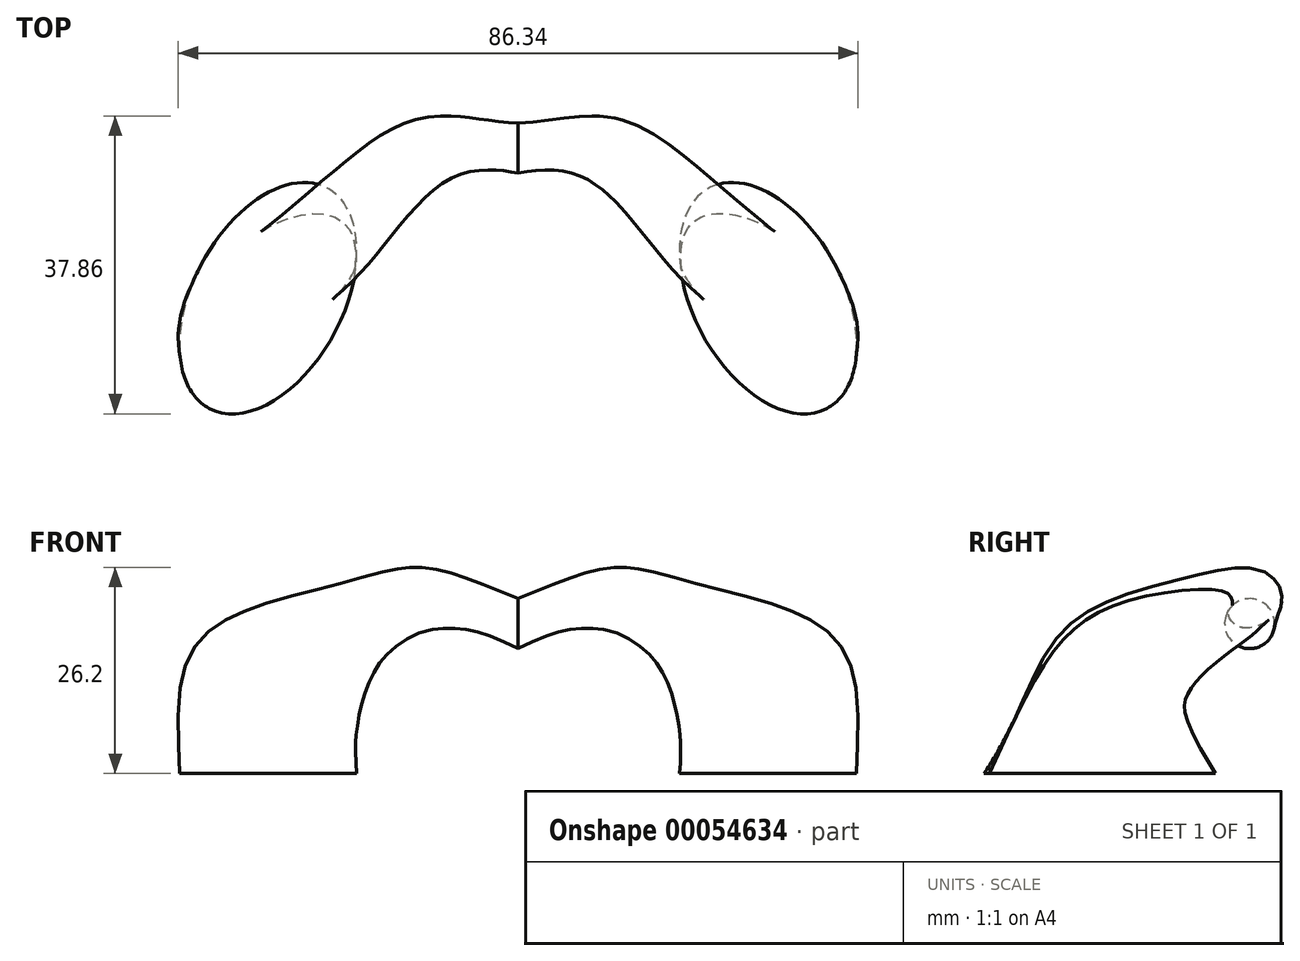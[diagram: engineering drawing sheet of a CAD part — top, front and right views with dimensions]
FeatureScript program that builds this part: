
annotation { "Feature Type Name" : "Feature", "Feature Type Description" : "" }
export const myFeature = defineFeature(function(context is Context, id is Id, definition is map)
    precondition{}
    {
        {
            var Q0;
            Q0=qCreatedBy(makeId("Top.planeOp"),FACE);
            var sketch = newSketch(context, id + "F0", { "sketchPlane" : qUnion([Q0])});
            skEllipse(sketch, "E0", {"center": v(31.75, -19.05) * mm, "majorRadius": 15.88 * mm, "minorRadius": 9.53 * mm, "majorAxis": v(0.47, -0.88)});
            skSolve(sketch);
        }
        {
            var Q0;
            Q0=qCreatedBy(makeId("Right.planeOp"),FACE);
            var sketch = newSketch(context, id + "F1", { "sketchPlane" : qUnion([Q0])});
            skCircle(sketch, "E1", {"center": v(0, 19.05) * mm, "radius": 3.18 * mm});
            skSolve(sketch);
        }
        {
            var Q0;
            Q0=qCreatedBy(makeId("Right.planeOp"),FACE);
            var Q1;
            Q1=qCreatedBy(makeId("Top.planeOp"),FACE);
            cPlane(context, id + "F2", {"entities" : qUnion([Q0, Q1]), "cplaneType" : CPlaneType.MID_PLANE, "offset" : 25.4 * mm, "width" : 152.4 * mm, "height" : 152.4 * mm});
        }
        {
            var Q0;
            Q0=qCreatedBy(id+"F2.planeOp",FACE);
            var sketch = newSketch(context, id + "F3", { "sketchPlane" : qUnion([Q0])});
            skEllipse(sketch, "E2", {"center": v(-7.75, 28.08) * mm, "majorRadius": 8.5 * mm, "minorRadius": 5.1 * mm, "majorAxis": v(-0.94, 0.35)});
            skSolve(sketch);
        }
        {
            var Q0;
            Q0=qCreatedBy(makeId("Right.planeOp"),FACE);
            var Q1;
            Q1=qCreatedBy(id+"F2.planeOp",FACE);
            cPlane(context, id + "F4", {"entities" : qUnion([Q0, Q1]), "cplaneType" : CPlaneType.MID_PLANE, "offset" : 152.4 * mm, "flipAlignment" : true, "width" : 152.4 * mm, "height" : 152.4 * mm});
        }
        {
            var Q0;
            Q0=qCreatedBy(id+"F4.planeOp",FACE);
            var sketch = newSketch(context, id + "F5", { "sketchPlane" : qUnion([Q0])});
            skCircle(sketch, "E3", {"center": v(0, 24.07) * mm, "radius": 4.1 * mm});
            skSolve(sketch);
        }
        {
            var Q0;
            Q0=qCreatedBy(id+"F2.planeOp",FACE);
            var Q1;
            Q1=qCreatedBy(makeId("Top.planeOp"),FACE);
            cPlane(context, id + "F6", {"entities" : qUnion([Q0, Q1]), "cplaneType" : CPlaneType.MID_PLANE, "offset" : 152.4 * mm, "width" : 152.4 * mm, "height" : 152.4 * mm});
        }
        {
            var Q0;
            Q0=qCreatedBy(id+"F6.planeOp",FACE);
            var sketch = newSketch(context, id + "F7", { "sketchPlane" : qUnion([Q0])});
            skEllipse(sketch, "E4", {"center": v(32.8, 16.93) * mm, "majorRadius": 12.65 * mm, "minorRadius": 6.7 * mm, "majorAxis": v(0.83, 0.56)});
            skSolve(sketch);
        }
        {
            var Q0;
            Q0=makeQuery(id+"F0.imprint","IMPRINT",FACE,{"disambiguationData":[TD([[makeQuery(id+"F0.imprint","IMPRINT",EDGE,{"derivedFrom":sQuery(id+"F0.wireOp",EDGE,"E0")}),1.0]])]});
            var Q1;
            Q1=makeQuery(id+"F7.imprint","IMPRINT",FACE,{"disambiguationData":[TD([[makeQuery(id+"F7.imprint","IMPRINT",EDGE,{"derivedFrom":sQuery(id+"F7.wireOp",EDGE,"E4")}),1.0]])]});
            var Q2;
            Q2=makeQuery(id+"F3.imprint","IMPRINT",FACE,{"disambiguationData":[TD([[makeQuery(id+"F3.imprint","IMPRINT",EDGE,{"derivedFrom":sQuery(id+"F3.wireOp",EDGE,"E2")}),1.0]])]});
            var Q3;
            Q3=makeQuery(id+"F5.imprint","IMPRINT",FACE,{"disambiguationData":[TD([[makeQuery(id+"F5.imprint","IMPRINT",EDGE,{"derivedFrom":sQuery(id+"F5.wireOp",EDGE,"E3")}),1.0]])]});
            var Q4;
            Q4=makeQuery(id+"F1.imprint","IMPRINT",FACE,{"disambiguationData":[TD([[makeQuery(id+"F1.imprint","IMPRINT",EDGE,{"derivedFrom":sQuery(id+"F1.wireOp",EDGE,"E1")}),1.0]])]});
            loft(context, id + "F8", {"sheetProfilesArray" : [{ "sheetProfileEntities" : qUnion([Q0]) }, { "sheetProfileEntities" : qUnion([Q1]) }, { "sheetProfileEntities" : qUnion([Q2]) }, { "sheetProfileEntities" : qUnion([Q3]) }, { "sheetProfileEntities" : qUnion([Q4]) }]});
        }
        {
            var Q0;
            Q0=makeQuery(id+"F8.opLoft","SWEPT_BODY",BODY,{"disambiguationData":[OSD([makeQuery(id+"F0.imprint","IMPRINT",FACE,{"disambiguationData":[TD([[makeQuery(id+"F0.imprint","IMPRINT",EDGE,{"derivedFrom":sQuery(id+"F0.wireOp",EDGE,"E0")}),1.0]])]}),makeQuery(id+"F1.imprint","IMPRINT",FACE,{"disambiguationData":[TD([[makeQuery(id+"F1.imprint","IMPRINT",EDGE,{"derivedFrom":sQuery(id+"F1.wireOp",EDGE,"E1")}),1.0]])]}),sQuery(id+"F3.wireOp",EDGE,"E2"),sQuery(id+"F5.wireOp",EDGE,"E3"),sQuery(id+"F7.wireOp",EDGE,"E4")])]});
            var Q1;
            Q1=qCreatedBy(makeId("Right.planeOp"),FACE);
            mirror(context, id + "F9", {"operationType" : NewBodyOperationType.ADD, "entities" : qUnion([Q0]), "mirrorPlane" : qUnion([Q1])});
        }
    });
